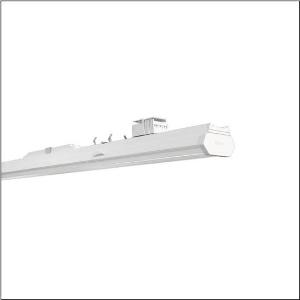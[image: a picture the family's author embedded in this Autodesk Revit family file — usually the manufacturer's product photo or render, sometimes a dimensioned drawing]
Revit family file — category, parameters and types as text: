
# Revit family: licross_r__11_protected_ho_51td12dn4fxm_db4e
name_source: partatom
category: Lighting Fixtures
units: mm (PartAtom-declared; Revit-internal decimal feet)

## family parameters
Cut with Voids When Loaded = No
Host = Face
Light Source = No
Part Type = Normal
Room Calculation Point = No
Round Connector Dimension = Use Diameter
Shared = No

## types (1)
- --- (1 x LED, 15270 lm, 87.3 W, 4000K)
    Apparent Load = 87 VA
    CIE Flux Codes = 70 91 97 98 100
    Color Rendering = 80
    Color Temperature = 4000K
    Default Elevation = 1800 mm
    Description = Licross® 11 Protected HO, luminaire insert, of sheet steel, galvanised, coil coated, white, length: 1.500mm, width: 90mm, height: 101mm, LED rated luminous flux: 15.270lm, light colour: 840, control gear: DALI 2, with plug, 5-pole, with phase selection, mains connection: 220..240V, AC, 50/60Hz, rated input power: 87W, halogen-free wiring, primary optical cover: cover, of PMMA, light emission: direct distribution, primary light characteristic: symmetric, protection rating (complete): IP54, insulation class (complete): insulation class I (protective earthing), certification: CE, ENEC, VDE, UKCA, protection symbol: D if used in an environment with non-conductive dust loads with corresponding accessories, impact resistance: IK06, permissible ambient temperature for indoor applications: -25..+30°C, corresponds to IFS (International Featured Standards) requirements for safety and quality in the food industry, reducing of maximum allowable ambient temperature of 5°C with ceiling mounting, LABS conformity tested according to VDMA 24364:2018-05, packaging unit: 1 piece
    Height = 92 mm
    Lamp = 1 x LED
    Lamp Light Flux = 15270 lm
    Lamp Power = 87.3 W
    Lamp count = 1
    Length = 1500 mm
    Luminous efficacy = 175 lm/W
    Manufacturer = Siteco
    ModVariant = No
    Model = 51TD12DN4FXM
    Mounting Place = Ceiling
    Mounting Type = Pendant
    Number of Poles = 1
    OnlyDefault = Yes
    Power Factor = 1
    Product Name = Licross® 11 Protected HO
    Product group = luminaire insert
    ProductGroupID = 901
    Protection Class = Protection class I
    Protection Degree = IP 54
    RLX_Detail_Level = 1
    RLX_Emergency_Light_Flux = 0 lm
    RLX_Emergency_Type = 0
    RLX_Emergency_Type_DB = No
    RlxData = <blob elided: 24429 chars, md5=ef329886>
    Socket = socket
    Standby Power = 0 W
    System Light Flux = 15270 lm
    System Power = 87 W
    Type Comments = factory setting: luminous flux: 100 % | dim-lin: 254 | 589 mA
    Type Image = l_1256145.jpg
    URL = http://relux.com
    VarID = @adj_070071
    Voltage = 0 V
    Weight = 0.00 kg
    Width = 88 mm

## geometry (parser evidence)
native form markers: Blend x4, Sweep x11
no freeform markers — native parametric forms only
